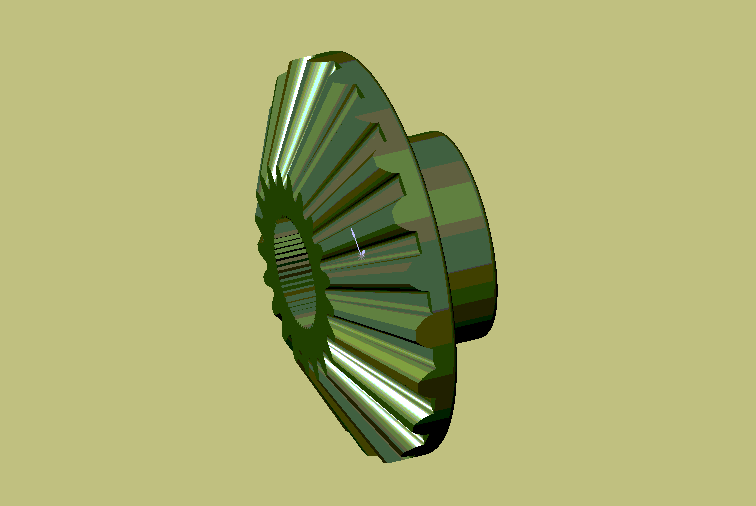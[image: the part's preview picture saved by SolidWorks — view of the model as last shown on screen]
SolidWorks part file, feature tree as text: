
SOLIDWORKS PART (.sldprt)
format: sldprt  version: not decoded by parser v0  size: 851,968 bytes
history: native  units: mm
features: sketch x22, plane x4, pattern_circular x2, cut_extrude x2, extrude x2, material x1, fillet x1 + 1 further entry (+9 scaffold rows collapsed)
feature tree (44):
  scaffold x9  (default folders/planes/origin — collapsed)
  material  "Matériau <non spécifié>"
  plane  "Plane1"
  plane  "Plane2"
  plane  "Plane3"
  "Famille de pièces"
  sketch  "Esquisse1"  dims[c1.D2=9.45mm c1.D1=42.0mm c2.D1=~8.571429deg]
  sketch  "Esquisse2"  dims[c1.D2=~9.260032mm c1.D1=37.0mm c2.D1=~9.341103deg]
  sketch  "Esquisse3"  dims[c1.D2=~9.070064mm c1.D1=33.0mm c2.D1=~9.94451deg]
  sketch  "Esquisse4"  dims[c1.D2=~8.880095mm c1.D1=30.0mm c2.D1=~10.279345deg]
  sketch  "Esquisse5"  dims[c1.D2=9.75mm c1.D1=46.0mm c2.D1=~7.103749deg]
  sketch  "Esquisse6"  dims[c1.D2=10.05mm c1.D1=50.0mm c2.D1=~5.394281deg]
  sketch  "Esquisse7"  dims[c1.D2=10.35mm c1.D1=54.0mm c2.D1=~3.490942deg]
  plane  "Plan1"  Offset=3mm
  sketch  "Esquisse8"  dims[c1.D2=~4.253848mm c1.D1=18.0mm c2.D1=~8.571429deg]
  sketch  "Esquisse9"  dims[c1.D2=~4.168335mm c1.D1=15.0mm c2.D1=~9.341103deg]
  sketch  "Esquisse10"  dims[c1.D2=~4.082822mm c1.D1=13.0mm c2.D1=~9.94451deg]
  sketch  "Esquisse11"  dims[c1.D2=~3.997309mm c1.D1=12.0mm c2.D1=~10.279345deg]
  sketch  "Esquisse12"  dims[c1.D2=~4.38889mm c1.D1=20.0mm c2.D1=~7.103749deg]
  sketch  "Esquisse13"  dims[c1.D2=~4.523933mm c1.D1=21.0mm c2.D1=~5.394281deg]
  sketch  "Esquisse14"  dims[c1.D2=~4.658976mm c1.D1=22.0mm c2.D1=~3.490942deg]
  sketch  "Esquisse15"  dims[c1.D2=8.325mm c1.D1=23.0mm c2.D1=~10.279345deg]
  sketch  "Esquisse16"  dims[c1.D2=~3.747437mm c1.D1=10.0mm c2.D1=~10.279345deg]
  sketch  "Esquisse17"  dims[D1=16.65mm]
  sketch  "Esquisse18"  dims[D1=~7.494874mm]
  fillet  "Congé1"  Radius=0.25mm
  pattern_circular  "Répétition circulaire1"  Count=21 Angle=360deg
  sketch  "Esquisse19"  dims[c1.D1=5.0mm c1.D4=4.75mm c1.D2=3.0mm c2.D2=6.0deg c2.D3=~4.123106mm c3.D3=3.0deg]
  sketch  "Esquisse20"  dims[D1=17.5mm]
  cut_extrude  "Enlèv. mat.-Extru.1"  [1 undecoded]
  sketch  "Esquisse21"  dims[D1=17.5mm]
  extrude  "Boss.-Extru.1"  Depth=1mm
  sketch  "Esquisse22"  dims[D1=9.0mm]
  extrude  "Boss.-Extru.2"  Depth=3.5mm
  cut_extrude  "Enlèv. mat.-Extru.3"  [1 undecoded]
  pattern_circular  "Congé2"  [2 undecoded]
decode coverage: 26 of 29 modeling features carry decoded parameters; 1 rows unclassified (native names shown)
note: ~ marks probable driven/reference dimensions
note: 4 parameter values undecoded
note: suppression state not decoded; provenance and decode notes live in map.json
